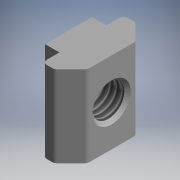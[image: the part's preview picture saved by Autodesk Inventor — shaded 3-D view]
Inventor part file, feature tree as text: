
AUTODESK INVENTOR PART (.ipt)
format: ipt  version: 2017.3 (Build 213256000, 256)  size: 125,440 bytes
history: native  units: mm (DEFAULTED — no unit token found)
features: other x21, sketch x2, extrude x1, revolve x1, thread x1
ambient origin geometry x8: Origin, YZ Plane, XZ Plane, XY Plane, X Axis, Y Axis, Z Axis, Center Point
bodies: Solid1 (feature_tree)
feature tree (26):
  extrude  "Extrusion1"  TaperAngle=360.0deg  [1 undecoded]
  revolve  "Revolution1"  [1 undecoded]
  thread  "Thread1"  [1 undecoded]
  other  "nut_XY"
  other  "nut_YZ"
  other  "nut_ZX"
  other  "nut_X"
  other  "nut_Y"
  other  "nut_Z"
  other  "nut_Center"
  other  "to_bolt_XY"
  other  "to_bolt_YZ"
  other  "to_bolt_ZX"
  other  "to_bolt_X"
  other  "to_bolt_Y"
  other  "to_bolt_Z"
  other  "to_bolt_Center"
  other  "to_frames_XY"
  other  "to_frames_YZ"
  other  "to_frames_ZX"
  other  "to_frames_X"
  other  "to_frames_Y"
  other  "to_frames_Z"
  other  "to_frames_Center"
  sketch  "Sketch_1"  dims[d0=17.0mm d1=0.0mm d2=360.0deg]
  sketch  "Sketch_5"  dims[d3=7.647mm d4=0.0mm d5=0.0mm d6=0.0mm]
note: 3 required parameter values undecoded (feature->parameter linkage not recoverable at this tier; creation-order binding heuristic only, values carry confidence <= 0.55)